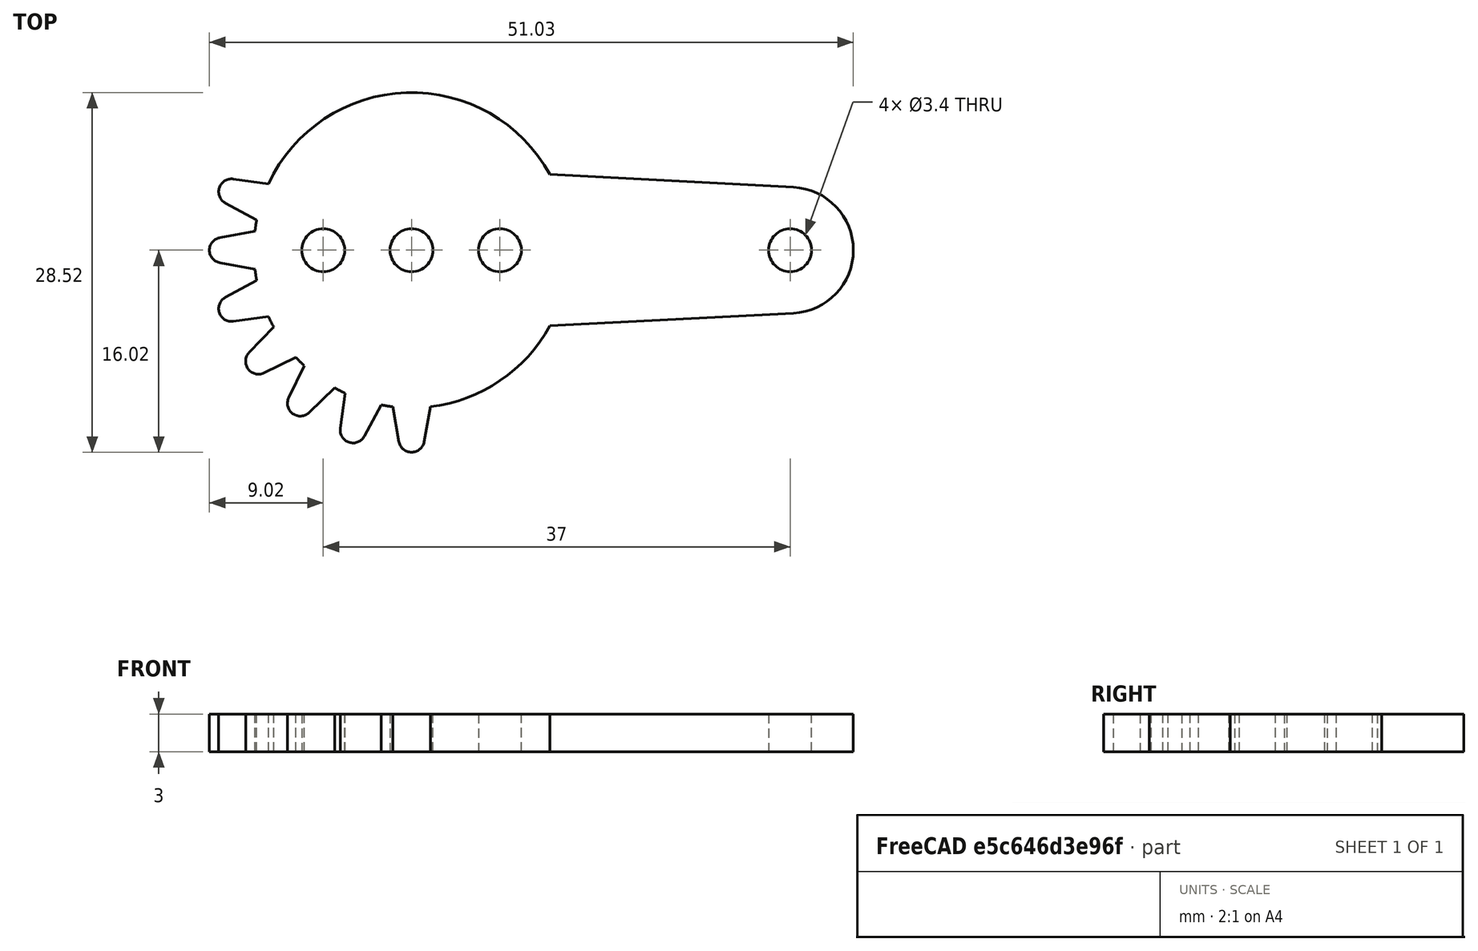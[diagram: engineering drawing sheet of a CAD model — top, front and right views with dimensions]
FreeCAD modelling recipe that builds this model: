
FCSTD DOCUMENT  (FreeCAD 0.19R24276 (Git))
Label: part3_2
License: All rights reserved
LicenseURL: http://en.wikipedia.org/wiki/All_rights_reserved
objects: Sketcher::SketchObject×1, PartDesign::Pad×1, PartDesign::Body×1
note: 4 computed .brp shape members not serialized (recipe doc carries the construction recipe); baked Part::Feature solids carry a one-line shape summary decoded from their .brp

FEATURE [Sketcher::SketchObject] Sketch
  FullyConstrained = false
  MapMode = 5
  Support = -> [XY_Plane]
  sketch-geometry (45):
    g0: Circle CenterX=0 CenterY=0 CenterZ=0 NormalX=0 NormalY=0 NormalZ=1 AngleXU=0 Radius=1.7
    g1: Circle CenterX=7 CenterY=0 CenterZ=0 NormalX=0 NormalY=0 NormalZ=1 AngleXU=0 Radius=1.7
    g2: Circle CenterX=-7 CenterY=0 CenterZ=0 NormalX=0 NormalY=0 NormalZ=1 AngleXU=0 Radius=1.7
    g3: Circle CenterX=30 CenterY=-4e-16 CenterZ=0 NormalX=0 NormalY=0 NormalZ=1 AngleXU=0 Radius=1.7
    g4: ArcOfCircle CenterX=0 CenterY=0 CenterZ=0 NormalX=0 NormalY=0 NormalZ=1 AngleXU=0 Radius=12.5 StartAngle=3.57604 EndAngle=3.64962
    g5: LineSegment StartX=10.9659 StartY=6 StartZ=0 EndX=30.2592 EndY=5 EndZ=0
    g6: ArcOfCircle CenterX=30 CenterY=-4e-16 CenterZ=0 NormalX=0 NormalY=0 NormalZ=1 AngleXU=0 Radius=5.00671 StartAngle=4.76417 EndAngle=7.8022
    g7: LineSegment StartX=30.2592 StartY=-5 StartZ=0 EndX=10.9659 EndY=-6 EndZ=0
    g8: LineSegment StartX=0 StartY=-12.5 StartZ=0 EndX=0 EndY=-6.18736 EndZ=0
    g9: LineSegment StartX=0 StartY=0 StartZ=0 EndX=-3.86271 EndY=-11.8882 EndZ=0
    g10: LineSegment StartX=0 StartY=0 StartZ=0 EndX=-7.34732 EndY=-10.1127 EndZ=0
    g11: LineSegment StartX=0 StartY=0 StartZ=0 EndX=-10.1127 EndY=-7.34732 EndZ=0
    g12: LineSegment StartX=0 StartY=0 StartZ=0 EndX=-11.8882 EndY=-3.86271 EndZ=0
    g13: LineSegment StartX=-11.3388 StartY=5.26138 StartZ=0 EndX=-14.1285 EndY=5.64207 EndZ=0
    g14: ArcOfCircle CenterX=-14.2658 CenterY=4.63525 CenterZ=0 NormalX=0 NormalY=0 NormalZ=1 AngleXU=0 Radius=1.01615 StartAngle=1.43517 EndAngle=4.2197
    g15: LineSegment StartX=-14.7465 StartY=3.73996 StartZ=0 EndX=-12.2658 EndY=2.40822 EndZ=0
    g16: LineSegment StartX=-12.4097 StartY=1.5 StartZ=0 EndX=-15.1805 EndY=1 EndZ=0
    g17: ArcOfCircle CenterX=-15 CenterY=1.3e-15 CenterZ=0 NormalX=0 NormalY=0 NormalZ=1 AngleXU=0 Radius=1.01615 StartAngle=1.74933 EndAngle=4.53386
    g18: LineSegment StartX=-15.1805 StartY=-1 StartZ=0 EndX=-12.4097 EndY=-1.5 EndZ=0
    g19: LineSegment StartX=-12.2658 StartY=-2.40822 StartZ=0 EndX=-14.7465 EndY=-3.73996 EndZ=0
    g20: ArcOfCircle CenterX=-14.2658 CenterY=-4.63525 CenterZ=0 NormalX=0 NormalY=0 NormalZ=1 AngleXU=0 Radius=1.01615 StartAngle=2.06349 EndAngle=4.84802
    g21: LineSegment StartX=-14.1285 StartY=-5.64207 StartZ=0 EndX=-11.3388 EndY=-5.26138 EndZ=0
    g22: LineSegment StartX=-10.9213 StartY=-6.0807 StartZ=0 EndX=-12.869 EndY=-8.11383 EndZ=0
    g23: ArcOfCircle CenterX=-12.1353 CenterY=-8.81678 CenterZ=0 NormalX=0 NormalY=0 NormalZ=1 AngleXU=0 Radius=1.01615 StartAngle=2.37765 EndAngle=5.16217
    g24: LineSegment StartX=-11.6935 StartY=-9.73186 StartZ=0 EndX=-9.15796 EndY=-8.50775 EndZ=0
    g25: LineSegment StartX=-8.50775 StartY=-9.15796 StartZ=0 EndX=-9.73186 EndY=-11.6935 EndZ=0
    g26: ArcOfCircle CenterX=-8.81678 CenterY=-12.1353 CenterZ=0 NormalX=0 NormalY=0 NormalZ=1 AngleXU=0 Radius=1.01615 StartAngle=2.69181 EndAngle=5.47633
    g27: LineSegment StartX=-8.11383 StartY=-12.869 StartZ=0 EndX=-6.0807 EndY=-10.9213 EndZ=0
    g28: LineSegment StartX=-5.26138 StartY=-11.3388 StartZ=0 EndX=-5.64207 EndY=-14.1285 EndZ=0
    g29: ArcOfCircle CenterX=-4.63525 CenterY=-14.2658 CenterZ=0 NormalX=0 NormalY=0 NormalZ=1 AngleXU=0 Radius=1.01615 StartAngle=3.00597 EndAngle=5.79049
    g30: LineSegment StartX=-3.73996 StartY=-14.7465 StartZ=0 EndX=-2.40822 EndY=-12.2658 EndZ=0
    g31: LineSegment StartX=-1.5 StartY=-12.4097 StartZ=0 EndX=-1 EndY=-15.1805 EndZ=0
    g32: ArcOfCircle CenterX=-3.522e-13 CenterY=-15 CenterZ=0 NormalX=0 NormalY=0 NormalZ=1 AngleXU=0 Radius=1.01615 StartAngle=3.32013 EndAngle=6.10465
    g33: LineSegment StartX=1 StartY=-15.1805 StartZ=0 EndX=1.5 EndY=-12.4097 EndZ=0
    g34: Circle CenterX=0 CenterY=0 CenterZ=0 NormalX=0 NormalY=0 NormalZ=1 AngleXU=0 Radius=12.5
    g35: ArcOfCircle CenterX=0 CenterY=0 CenterZ=0 NormalX=0 NormalY=0 NormalZ=1 AngleXU=0 Radius=12.5 StartAngle=3.8902 EndAngle=3.96378
    g36: ArcOfCircle CenterX=0 CenterY=0 CenterZ=0 NormalX=0 NormalY=0 NormalZ=1 AngleXU=0 Radius=12.5 StartAngle=4.20436 EndAngle=4.27794
    g37: ArcOfCircle CenterX=0 CenterY=0 CenterZ=0 NormalX=0 NormalY=0 NormalZ=1 AngleXU=0 Radius=12.5 StartAngle=4.51852 EndAngle=4.5921
    g38: LineSegment StartX=0 StartY=0 StartZ=0 EndX=0 EndY=-12.5 EndZ=0
    g39: ArcOfCircle CenterX=0 CenterY=0 CenterZ=0 NormalX=0 NormalY=0 NormalZ=1 AngleXU=0 Radius=12.5 StartAngle=4.83268 EndAngle=5.78253
    g40: LineSegment StartX=0 StartY=0 StartZ=0 EndX=-12.5 EndY=1e-15 EndZ=0
    g41: LineSegment StartX=0 StartY=0 StartZ=0 EndX=-11.8882 EndY=3.86271 EndZ=0
    g42: ArcOfCircle CenterX=0 CenterY=0 CenterZ=0 NormalX=0 NormalY=0 NormalZ=1 AngleXU=0 Radius=12.5 StartAngle=2.94772 EndAngle=3.0213
    g43: ArcOfCircle CenterX=0 CenterY=0 CenterZ=0 NormalX=0 NormalY=0 NormalZ=1 AngleXU=0 Radius=12.5 StartAngle=3.26188 EndAngle=3.33546
    g44: ArcOfCircle CenterX=0 CenterY=0 CenterZ=0 NormalX=0 NormalY=0 NormalZ=1 AngleXU=0 Radius=12.5 StartAngle=0.500655 EndAngle=2.70714
  constraints (134):
    c: Coincident(g0,g-1)
    c: PointOnObject(g1,g-1)
    c: Equal(g2,g0)
    c: Equal(g2,g1)
    c: Equal(g2,g3)
    c: Diameter(g2) = 3.4
    c: Symmetric(g2,g1,g0)
    c: DistanceX(g0,g1) = 7
    c: DistanceX(g0,g3) = 30
    c: Coincident(g4,g0)
    c: Diameter(g4) = 25
    c: PointOnObject(g5,g4)
    c: Tangent(g5,g6) = 1.5708
    c: Tangent(g6,g7) = 1.5708
    c: DistanceY(g6,g5) = 10
    c: Symmetric(g5,g6,g-1)
    c: Symmetric(g5,g7,g-1)
    c: Coincident(g6,g3)
    c: DistanceY(g7,g5) = 12
    c: PointOnObject(g8,g4)
    c: PointOnObject(g8,g-2)
    c: Vertical(g8)
    c: PointOnObject(g9,g4)
    c: PointOnObject(g10,g4)
    c: Angle(g10,g9) = 0.314159
    c: Angle(g11,g10) = 0.314159
    c: Angle(g12,g11) = 0.314159
    c: PointOnObject(g13,g4)
    c: Tangent(g13,g14) = -1.5708
    c: Tangent(g14,g15) = -1.5708
    c: Equal(g13,g15)
    c: PointOnObject(g15,g4)
    c: Distance(g14,g13) = 2
    c: Distance(g15,g13) = 3
    c: PointOnObject(g16,g4)
    c: Tangent(g16,g17) = -1.5708
    c: Tangent(g17,g18) = -1.5708
    c: Equal(g16,g18)
    c: PointOnObject(g18,g4)
    c: Distance(g16,g18) = 3
    c: Distance(g16,g17) = 2
    c: Tangent(g19,g20) = -1.5708
    c: Tangent(g20,g21) = -1.5708
    c: Equal(g19,g21)
    c: PointOnObject(g20,g12)
    c: Distance(g19,g21) = 3
    c: Distance(g20,g12) = 2.5
    c: Distance(g19,g20) = 2
    c: Tangent(g22,g23) = -1.5708
    c: Tangent(g23,g24) = -1.5708
    c: PointOnObject(g25,g4)
    c: Tangent(g25,g26) = -1.5708
    c: Tangent(g26,g27) = -1.5708
    c: PointOnObject(g28,g4)
    c: Tangent(g28,g29) = -1.5708
    c: Tangent(g29,g30) = -1.5708
    c: PointOnObject(g31,g4)
    c: Tangent(g31,g32) = -1.5708
    c: Tangent(g32,g33) = -1.5708
    c: PointOnObject(g23,g11)
    c: PointOnObject(g26,g10)
    c: PointOnObject(g29,g9)
    c: PointOnObject(g30,g4)
    c: PointOnObject(g24,g4)
    c: Equal(g22,g24)
    c: Equal(g25,g27)
    c: Equal(g28,g30)
    c: Equal(g31,g33)
    c: Distance(g22,g24) = 3
    c: Distance(g25,g27) = 3
    c: PointOnObject(g27,g4)
    c: Distance(g28,g30) = 3
    c: Distance(g31,g33) = 3
    c: Distance(g23,g11) = 2.5
    c: Distance(g26,g10) = 2.5
    c: Distance(g29,g9) = 2.5
    c: Distance(g22,g23) = 2
    c: Distance(g25,g26) = 2
    c: Distance(g28,g29) = 2
    c: Distance(g31,g32) = 2
    c: Coincident(g34,g0)
    c: PointOnObject(g31,g34)
    c: Coincident(g12,g0)
    c: Coincident(g43,g19)
    c: Coincident(g4,g21)
    c: Distance(g12,g0) = 12.5
    c: Coincident(g11,g0)
    c: Equal(g4,g35)
    c: Coincident(g4,g22)
    c: Coincident(g4,g35)
    c: PointOnObject(g35,g24)
    c: Equal(g12,g11)
    c: Coincident(g10,g0)
    c: Equal(g35,g36)
    c: PointOnObject(g35,g25)
    c: Coincident(g35,g36)
    c: PointOnObject(g36,g27)
    c: Coincident(g9,g0)
    c: Equal(g36,g37)
    c: PointOnObject(g36,g28)
    c: Coincident(g36,g37)
    c: PointOnObject(g37,g30)
    c: Coincident(g38,g0)
    c: Symmetric(g31,g33,g38)
    c: Distance(g38,g32) = 2.5
    c: Equal(g37,g39)
    c: PointOnObject(g37,g31)
    c: Coincident(g37,g39)
    c: PointOnObject(g39,g33)
    c: Equal(g12,g38)
    c: Coincident(g40,g0)
    c: PointOnObject(g40,g39)
    c: PointOnObject(g41,g34)
    c: Coincident(g41,g0)
    c: Distance(g41,g14) = 2.5
    c: Distance(g40,g17) = 2.5
    c: Equal(g39,g42)
    c: PointOnObject(g44,g13)
    c: Coincident(g39,g42)
    c: PointOnObject(g42,g15)
    c: Equal(g42,g43)
    c: PointOnObject(g42,g16)
    c: Coincident(g42,g43)
    c: PointOnObject(g43,g18)
    c: Angle(g40,g12) = 0.314159
    c: Angle(g41,g40) = 0.314159
    c: PointOnObject(g17,g40)
    c: PointOnObject(g14,g41)
    c: Equal(g39,g44)
    c: PointOnObject(g44,g5)
    c: Coincident(g39,g44)
    c: PointOnObject(g39,g7)
    c: Angle(g9,g38) = 0.314159
    c: PointOnObject(g38,g8)
FEATURE [PartDesign::Pad] Pad
  Direction = (1,1,1)
  Length = 3
  Length2 = 100
  Profile = -> Sketch
  Type = 0
FEATURE [PartDesign::Body] Body
  Group = -> [Sketch,Pad]
  Origin = -> Origin
  Tip = -> Pad
